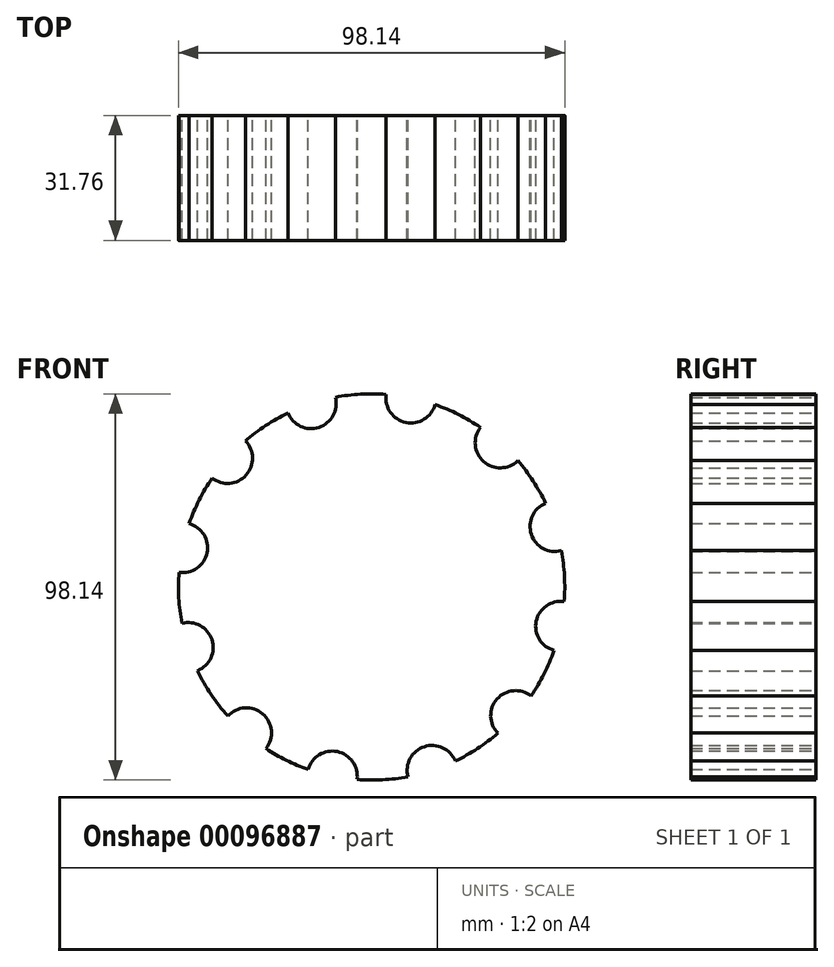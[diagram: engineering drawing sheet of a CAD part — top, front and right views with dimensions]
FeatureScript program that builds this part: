
annotation { "Feature Type Name" : "Feature", "Feature Type Description" : "" }
export const myFeature = defineFeature(function(context is Context, id is Id, definition is map)
    precondition{}
    {
        {
            var Q0;
            Q0=qCreatedBy(makeId("Front.planeOp"),FACE);
            var sketch = newSketch(context, id + "F0", { "sketchPlane" : qUnion([Q0])});
            skCircle(sketch, "E0.cCircle", {"center": v(0, 0) * mm, "radius": 49.07 * mm, "construction": true});
            skLineSegment(sketch, "E0.0", {"start": v(-32.67, -36.61) * mm, "end": v(-46.6, -15.37) * mm});
            skLineSegment(sketch, "E0.1", {"start": v(-46.6, -15.37) * mm, "end": v(-48.04, 9.99) * mm});
            skLineSegment(sketch, "E0.2", {"start": v(-48.04, 9.99) * mm, "end": v(-36.61, 32.67) * mm});
            skLineSegment(sketch, "E0.3", {"start": v(-36.61, 32.67) * mm, "end": v(-15.37, 46.6) * mm});
            skLineSegment(sketch, "E0.4", {"start": v(-15.37, 46.6) * mm, "end": v(9.99, 48.04) * mm});
            skLineSegment(sketch, "E0.5", {"start": v(9.99, 48.04) * mm, "end": v(32.67, 36.61) * mm});
            skLineSegment(sketch, "E0.6", {"start": v(32.67, 36.61) * mm, "end": v(46.6, 15.37) * mm});
            skLineSegment(sketch, "E0.7", {"start": v(46.6, 15.37) * mm, "end": v(48.04, -9.99) * mm});
            skLineSegment(sketch, "E0.8", {"start": v(48.04, -9.99) * mm, "end": v(36.61, -32.67) * mm});
            skLineSegment(sketch, "E0.9", {"start": v(36.61, -32.67) * mm, "end": v(15.37, -46.6) * mm});
            skLineSegment(sketch, "E0.10", {"start": v(15.37, -46.6) * mm, "end": v(-9.99, -48.04) * mm});
            skLineSegment(sketch, "E0.11", {"start": v(-9.99, -48.04) * mm, "end": v(-32.67, -36.61) * mm});
            skCircle(sketch, "E1", {"center": v(-48.04, 9.99) * mm, "radius": 6.35 * mm});
            skCircle(sketch, "E2", {"center": v(-15.37, 46.6) * mm, "radius": 6.35 * mm});
            skCircle(sketch, "E3", {"center": v(9.99, 48.04) * mm, "radius": 6.35 * mm});
            skCircle(sketch, "E4", {"center": v(-36.61, 32.67) * mm, "radius": 6.35 * mm});
            skCircle(sketch, "E5", {"center": v(32.67, 36.61) * mm, "radius": 6.35 * mm});
            skCircle(sketch, "E6", {"center": v(46.6, 15.37) * mm, "radius": 6.35 * mm});
            skCircle(sketch, "E7", {"center": v(48.04, -9.99) * mm, "radius": 6.35 * mm});
            skCircle(sketch, "E8", {"center": v(36.61, -32.67) * mm, "radius": 6.35 * mm});
            skCircle(sketch, "E9", {"center": v(15.37, -46.6) * mm, "radius": 6.35 * mm});
            skCircle(sketch, "E10", {"center": v(-9.99, -48.04) * mm, "radius": 6.35 * mm});
            skCircle(sketch, "E11", {"center": v(-31.8, -37.05) * mm, "radius": 6.35 * mm});
            skCircle(sketch, "E12", {"center": v(-46.6, -15.37) * mm, "radius": 6.35 * mm});
            skCircle(sketch, "E13", {"center": v(0, 0) * mm, "radius": 49.07 * mm});
            skSolve(sketch);
        }
        {
            var Q0;
            {var subQ36=sQuery(id+"F0.wireOp",EDGE,"E11");var subQ43=sQuery(id+"F0.wireOp",EDGE,"E0.0");var subQ44=makeQuery(id+"F0.imprint","INTERSECT",VERTEX,{"derivedFrom":[subQ43,subQ36]});Q0=makeQuery(id+"F0.imprint","IMPRINT",FACE,{"disambiguationData":[TD([[makeQuery(id+"F0.imprint","IMPRINT",EDGE,{"disambiguationData":[TD([[subQ44,-1.0]])],"derivedFrom":subQ43}),-1.0]])]});}
            var Q1;
            {var subQ0=sQuery(id+"F0.wireOp",EDGE,"E1");var subQ1=sQuery(id+"F0.wireOp",EDGE,"E0.2");var subQ2=makeQuery(id+"F0.imprint","INTERSECT",VERTEX,{"derivedFrom":[subQ1,subQ0]});Q1=makeQuery(id+"F0.imprint","IMPRINT",FACE,{"disambiguationData":[TD([[makeQuery(id+"F0.imprint","IMPRINT",EDGE,{"disambiguationData":[TD([[subQ2,-1.0]])],"derivedFrom":subQ1}),1.0]])]});}
            var Q2;
            {var subQ0=sQuery(id+"F0.wireOp",EDGE,"E4");var subQ1=sQuery(id+"F0.wireOp",EDGE,"E0.3");var subQ2=makeQuery(id+"F0.imprint","INTERSECT",VERTEX,{"derivedFrom":[subQ1,subQ0]});Q2=makeQuery(id+"F0.imprint","IMPRINT",FACE,{"disambiguationData":[TD([[makeQuery(id+"F0.imprint","IMPRINT",EDGE,{"disambiguationData":[TD([[subQ2,-1.0]])],"derivedFrom":subQ1}),1.0]])]});}
            var Q3;
            {var subQ0=sQuery(id+"F0.wireOp",EDGE,"E2");var subQ1=sQuery(id+"F0.wireOp",EDGE,"E0.4");var subQ2=makeQuery(id+"F0.imprint","INTERSECT",VERTEX,{"derivedFrom":[subQ1,subQ0]});Q3=makeQuery(id+"F0.imprint","IMPRINT",FACE,{"disambiguationData":[TD([[makeQuery(id+"F0.imprint","IMPRINT",EDGE,{"disambiguationData":[TD([[subQ2,-1.0]])],"derivedFrom":subQ1}),1.0]])]});}
            var Q4;
            {var subQ0=sQuery(id+"F0.wireOp",EDGE,"E3");var subQ1=sQuery(id+"F0.wireOp",EDGE,"E0.5");var subQ2=makeQuery(id+"F0.imprint","INTERSECT",VERTEX,{"derivedFrom":[subQ1,subQ0]});Q4=makeQuery(id+"F0.imprint","IMPRINT",FACE,{"disambiguationData":[TD([[makeQuery(id+"F0.imprint","IMPRINT",EDGE,{"disambiguationData":[TD([[subQ2,-1.0]])],"derivedFrom":subQ1}),1.0]])]});}
            var Q5;
            {var subQ0=sQuery(id+"F0.wireOp",EDGE,"E5");var subQ1=sQuery(id+"F0.wireOp",EDGE,"E0.6");var subQ2=makeQuery(id+"F0.imprint","INTERSECT",VERTEX,{"derivedFrom":[subQ1,subQ0]});Q5=makeQuery(id+"F0.imprint","IMPRINT",FACE,{"disambiguationData":[TD([[makeQuery(id+"F0.imprint","IMPRINT",EDGE,{"disambiguationData":[TD([[subQ2,-1.0]])],"derivedFrom":subQ1}),1.0]])]});}
            var Q6;
            {var subQ0=sQuery(id+"F0.wireOp",EDGE,"E6");var subQ1=sQuery(id+"F0.wireOp",EDGE,"E0.7");var subQ2=makeQuery(id+"F0.imprint","INTERSECT",VERTEX,{"derivedFrom":[subQ1,subQ0]});Q6=makeQuery(id+"F0.imprint","IMPRINT",FACE,{"disambiguationData":[TD([[makeQuery(id+"F0.imprint","IMPRINT",EDGE,{"disambiguationData":[TD([[subQ2,-1.0]])],"derivedFrom":subQ1}),1.0]])]});}
            var Q7;
            {var subQ0=sQuery(id+"F0.wireOp",EDGE,"E7");var subQ1=sQuery(id+"F0.wireOp",EDGE,"E0.8");var subQ2=makeQuery(id+"F0.imprint","INTERSECT",VERTEX,{"derivedFrom":[subQ1,subQ0]});Q7=makeQuery(id+"F0.imprint","IMPRINT",FACE,{"disambiguationData":[TD([[makeQuery(id+"F0.imprint","IMPRINT",EDGE,{"disambiguationData":[TD([[subQ2,-1.0]])],"derivedFrom":subQ1}),1.0]])]});}
            var Q8;
            {var subQ0=sQuery(id+"F0.wireOp",EDGE,"E8");var subQ1=sQuery(id+"F0.wireOp",EDGE,"E0.9");var subQ2=makeQuery(id+"F0.imprint","INTERSECT",VERTEX,{"derivedFrom":[subQ1,subQ0]});Q8=makeQuery(id+"F0.imprint","IMPRINT",FACE,{"disambiguationData":[TD([[makeQuery(id+"F0.imprint","IMPRINT",EDGE,{"disambiguationData":[TD([[subQ2,-1.0]])],"derivedFrom":subQ1}),1.0]])]});}
            var Q9;
            {var subQ0=sQuery(id+"F0.wireOp",EDGE,"E9");var subQ1=sQuery(id+"F0.wireOp",EDGE,"E0.10");var subQ2=makeQuery(id+"F0.imprint","INTERSECT",VERTEX,{"derivedFrom":[subQ1,subQ0]});Q9=makeQuery(id+"F0.imprint","IMPRINT",FACE,{"disambiguationData":[TD([[makeQuery(id+"F0.imprint","IMPRINT",EDGE,{"disambiguationData":[TD([[subQ2,-1.0]])],"derivedFrom":subQ1}),1.0]])]});}
            var Q10;
            {var subQ0=sQuery(id+"F0.wireOp",EDGE,"E10");var subQ1=sQuery(id+"F0.wireOp",EDGE,"E0.11");var subQ2=makeQuery(id+"F0.imprint","INTERSECT",VERTEX,{"derivedFrom":[subQ1,subQ0]});Q10=makeQuery(id+"F0.imprint","IMPRINT",FACE,{"disambiguationData":[TD([[makeQuery(id+"F0.imprint","IMPRINT",EDGE,{"disambiguationData":[TD([[subQ2,-1.0]])],"derivedFrom":subQ1}),1.0]])]});}
            var Q11;
            {var subQ0=sQuery(id+"F0.wireOp",EDGE,"E11");var subQ1=sQuery(id+"F0.wireOp",EDGE,"E0.0");var subQ2=makeQuery(id+"F0.imprint","INTERSECT",VERTEX,{"derivedFrom":[subQ1,subQ0]});Q11=makeQuery(id+"F0.imprint","IMPRINT",FACE,{"disambiguationData":[TD([[makeQuery(id+"F0.imprint","IMPRINT",EDGE,{"disambiguationData":[TD([[subQ2,-1.0]])],"derivedFrom":subQ1}),1.0]])]});}
            var Q12;
            {var subQ0=sQuery(id+"F0.wireOp",EDGE,"E12");var subQ1=sQuery(id+"F0.wireOp",EDGE,"E0.1");var subQ2=makeQuery(id+"F0.imprint","INTERSECT",VERTEX,{"derivedFrom":[subQ1,subQ0]});Q12=makeQuery(id+"F0.imprint","IMPRINT",FACE,{"disambiguationData":[TD([[makeQuery(id+"F0.imprint","IMPRINT",EDGE,{"disambiguationData":[TD([[subQ2,-1.0]])],"derivedFrom":subQ1}),1.0]])]});}
            extrude(context, id + "F1", {"entities" : qUnion([Q0, Q1, Q2, Q3, Q4, Q5, Q6, Q7, Q8, Q9, Q10, Q11, Q12]), "endBound" : BoundingType.SYMMETRIC, "depth" : 31.75 * mm});
        }
    });
